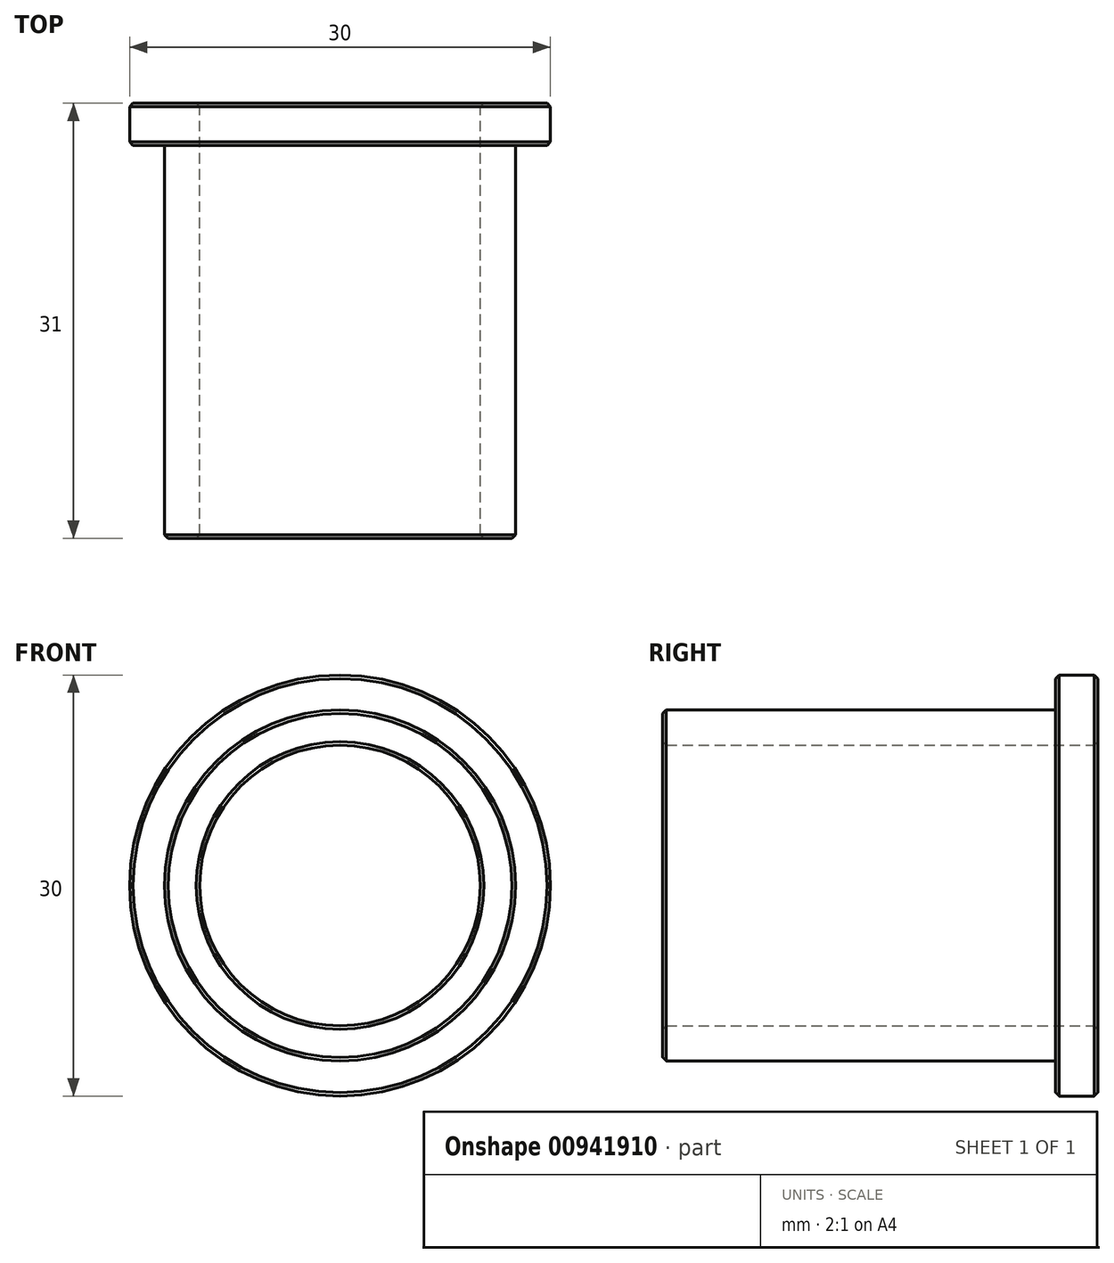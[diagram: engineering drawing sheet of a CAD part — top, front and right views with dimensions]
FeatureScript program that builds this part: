
annotation { "Feature Type Name" : "Feature", "Feature Type Description" : "" }
export const myFeature = defineFeature(function(context is Context, id is Id, definition is map)
    precondition{}
    {
        {
            var Q0;
            Q0=qCreatedBy(makeId("Front.planeOp"),FACE);
            var sketch = newSketch(context, id + "F0", { "sketchPlane" : qUnion([Q0])});
            skCircle(sketch, "E0", {"center": v(0, 0) * mm, "radius": 15 * mm});
            skCircle(sketch, "E1", {"center": v(0, 0) * mm, "radius": 12.5 * mm});
            skCircle(sketch, "E2", {"center": v(0, 0) * mm, "radius": 10 * mm});
            skSolve(sketch);
        }
        {
            var Q0;
            Q0=makeQuery(id+"F0.imprint","IMPRINT",FACE,{"disambiguationData":[TD([[makeQuery(id+"F0.imprint","IMPRINT",EDGE,{"derivedFrom":sQuery(id+"F0.wireOp",EDGE,"E0")}),1.0]])]});
            extrude(context, id + "F1", {"entities" : qUnion([Q0]), "depth" : 3 * mm, "offsetDistance" : 25 * mm});
        }
        {
            var Q0;
            Q0=makeQuery(id+"F0.imprint","IMPRINT",FACE,{"disambiguationData":[TD([[makeQuery(id+"F0.imprint","IMPRINT",EDGE,{"derivedFrom":sQuery(id+"F0.wireOp",EDGE,"E1")}),1.0]])]});
            extrude(context, id + "F2", {"entities" : qUnion([Q0]), "operationType" : NewBodyOperationType.ADD, "depth" : 31 * mm, "offsetDistance" : 25 * mm});
        }
        {
            var Q0;
            Q0=makeQuery(id+"F2.opExtrude","CAP_FACE",FACE,{"disambiguationData":[OSD([sQuery(id+"F0.wireOp",EDGE,"E1"),sQuery(id+"F0.wireOp",EDGE,"E2")])],"isStart":false});
            var Q1;
            {var subQ0=sQuery(id+"F0.wireOp",EDGE,"E1");Q1=makeQuery(id+"F2.boolean.opBoolean","MERGE",FACE,{"derivedFrom":[makeQuery(id+"F1.opExtrude","CAP_FACE",FACE,{"disambiguationData":[OSD([sQuery(id+"F0.wireOp",EDGE,"E0"),subQ0])],"isStart":true}),makeQuery(id+"F2.opExtrude","CAP_FACE",FACE,{"disambiguationData":[OSD([subQ0,sQuery(id+"F0.wireOp",EDGE,"E2")])],"isStart":true})]});}
            var Q2;
            Q2=makeQuery(id+"F1.opExtrude","CAP_EDGE",EDGE,{"disambiguationData":[OSD([sQuery(id+"F0.wireOp",EDGE,"E0")])],"isStart":false});
            chamfer(context, id + "F3", {"entities" : qUnion([Q0, Q1, Q2]), "width" : 0.25 * mm, "tangentPropagation" : true});
        }
    });
